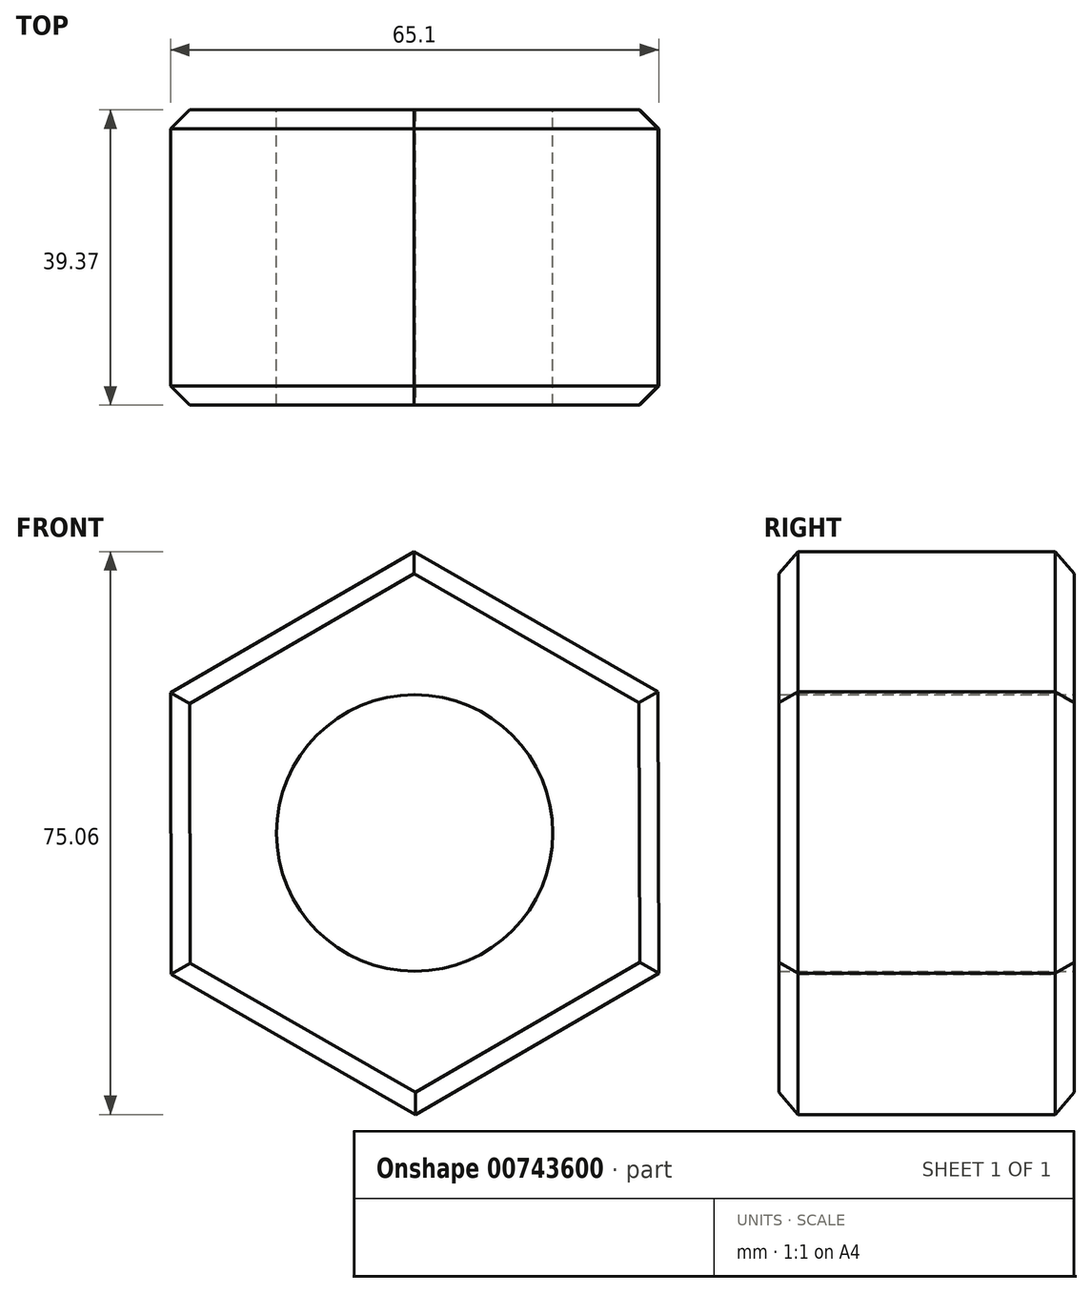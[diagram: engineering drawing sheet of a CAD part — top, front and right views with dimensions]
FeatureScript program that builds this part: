
annotation { "Feature Type Name" : "Feature", "Feature Type Description" : "" }
export const myFeature = defineFeature(function(context is Context, id is Id, definition is map)
    precondition{}
    {
        {
            var Q0;
            Q0=qCreatedBy(makeId("Front.planeOp"),FACE);
            var sketch = newSketch(context, id + "F0", { "sketchPlane" : qUnion([Q0])});
            skCircle(sketch, "E0.cCircle", {"center": v(0, 0) * mm, "radius": 32.5 * mm, "construction": true});
            skLineSegment(sketch, "E0.0", {"start": v(-0.1, 37.53) * mm, "end": v(32.46, 18.85) * mm});
            skLineSegment(sketch, "E0.1", {"start": v(32.46, 18.85) * mm, "end": v(32.55, -18.69) * mm});
            skLineSegment(sketch, "E0.2", {"start": v(32.55, -18.69) * mm, "end": v(0.1, -37.53) * mm});
            skLineSegment(sketch, "E0.3", {"start": v(0.1, -37.53) * mm, "end": v(-32.46, -18.85) * mm});
            skLineSegment(sketch, "E0.4", {"start": v(-32.46, -18.85) * mm, "end": v(-32.55, 18.69) * mm});
            skLineSegment(sketch, "E0.5", {"start": v(-32.55, 18.69) * mm, "end": v(-0.1, 37.53) * mm});
            skPoint(sketch, "E0.0.midPoint", {"position": v(16.18, 28.19) * mm});
            skCircle(sketch, "E1", {"center": v(0, 0) * mm, "radius": 18.42 * mm});
            skSolve(sketch);
        }
        {
            var Q0;
            Q0 = qSketchRegion(id + "F0", true);
            extrude(context, id + "F1", {"entities" : qUnion([Q0]), "depth" : 39.37 * mm, "offsetDistance" : 25.4 * mm});
        }
        {
            var Q0;
            Q0=makeQuery(id+"F1.opExtrude","CAP_EDGE",EDGE,{"disambiguationData":[OSD([sQuery(id+"F0.wireOp",EDGE,"E0.4")])],"isStart":true});
            var Q1;
            Q1=makeQuery(id+"F1.opExtrude","CAP_EDGE",EDGE,{"disambiguationData":[OSD([sQuery(id+"F0.wireOp",EDGE,"E0.3")])],"isStart":true});
            var Q2;
            Q2=makeQuery(id+"F1.opExtrude","CAP_EDGE",EDGE,{"disambiguationData":[OSD([sQuery(id+"F0.wireOp",EDGE,"E0.2")])],"isStart":true});
            var Q3;
            Q3=makeQuery(id+"F1.opExtrude","CAP_EDGE",EDGE,{"disambiguationData":[OSD([sQuery(id+"F0.wireOp",EDGE,"E0.1")])],"isStart":true});
            var Q4;
            Q4=makeQuery(id+"F1.opExtrude","CAP_EDGE",EDGE,{"disambiguationData":[OSD([sQuery(id+"F0.wireOp",EDGE,"E0.0")])],"isStart":true});
            var Q5;
            Q5=makeQuery(id+"F1.opExtrude","CAP_EDGE",EDGE,{"disambiguationData":[OSD([sQuery(id+"F0.wireOp",EDGE,"E0.5")])],"isStart":true});
            var Q6;
            Q6=makeQuery(id+"F1.opExtrude","CAP_EDGE",EDGE,{"disambiguationData":[OSD([sQuery(id+"F0.wireOp",EDGE,"E0.0")])],"isStart":false});
            var Q7;
            Q7=makeQuery(id+"F1.opExtrude","CAP_EDGE",EDGE,{"disambiguationData":[OSD([sQuery(id+"F0.wireOp",EDGE,"E0.5")])],"isStart":false});
            var Q8;
            Q8=makeQuery(id+"F1.opExtrude","CAP_EDGE",EDGE,{"disambiguationData":[OSD([sQuery(id+"F0.wireOp",EDGE,"E0.4")])],"isStart":false});
            var Q9;
            Q9=makeQuery(id+"F1.opExtrude","CAP_EDGE",EDGE,{"disambiguationData":[OSD([sQuery(id+"F0.wireOp",EDGE,"E0.3")])],"isStart":false});
            var Q10;
            Q10=makeQuery(id+"F1.opExtrude","CAP_EDGE",EDGE,{"disambiguationData":[OSD([sQuery(id+"F0.wireOp",EDGE,"E0.2")])],"isStart":false});
            var Q11;
            Q11=makeQuery(id+"F1.opExtrude","CAP_EDGE",EDGE,{"disambiguationData":[OSD([sQuery(id+"F0.wireOp",EDGE,"E0.1")])],"isStart":false});
            chamfer(context, id + "F2", {"entities" : qUnion([Q0, Q1, Q2, Q3, Q4, Q5, Q6, Q7, Q8, Q9, Q10, Q11]), "width" : 2.54 * mm, "tangentPropagation" : true});
        }
    });
